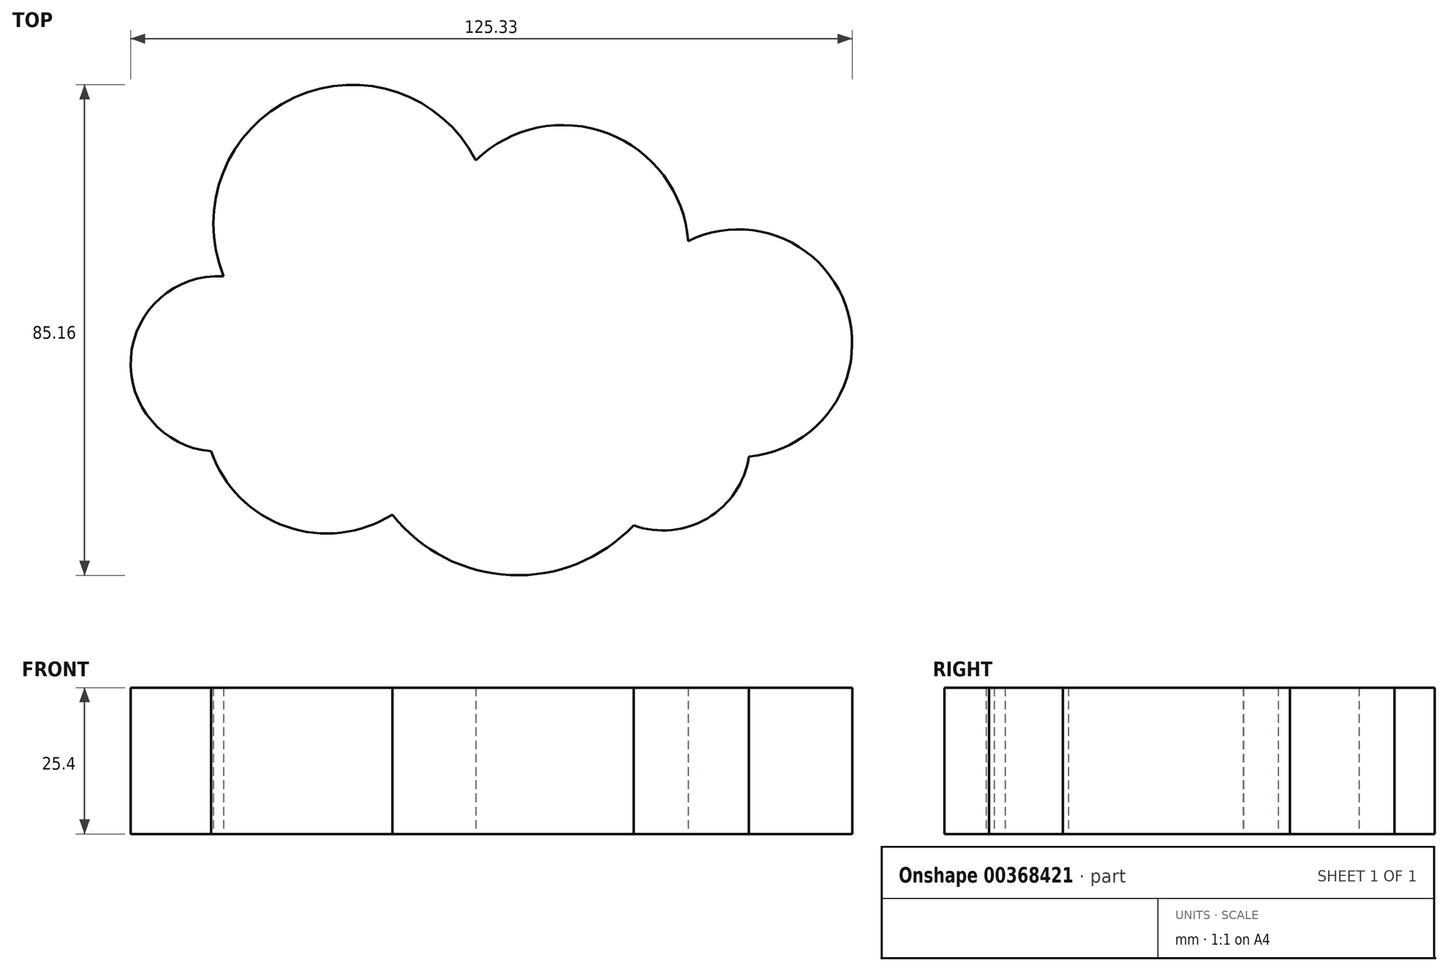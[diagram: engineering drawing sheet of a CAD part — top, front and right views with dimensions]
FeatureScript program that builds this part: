
annotation { "Feature Type Name" : "Feature", "Feature Type Description" : "" }
export const myFeature = defineFeature(function(context is Context, id is Id, definition is map)
    precondition{}
    {
        {
            var Q0;
            Q0=qCreatedBy(makeId("Top.planeOp"),FACE);
            var sketch = newSketch(context, id + "F0", { "sketchPlane" : qUnion([Q0])});
            skArc(sketch, "E0", {"start": v(-17.95, 29.07) * mm, "mid": v(-34.05, 14.96) * mm, "end": v(-20.13, -1.3) * mm});
            skArc(sketch, "E1", {"start": v(25.89, 49.22) * mm, "mid": v(-5.66, 60.1) * mm, "end": v(-17.95, 29.07) * mm});
            skArc(sketch, "E2", {"start": v(-20.13, -1.3) * mm, "mid": v(-7.03, -14.4) * mm, "end": v(11.37, -12.3) * mm});
            skArc(sketch, "E3", {"start": v(11.37, -12.3) * mm, "mid": v(31.9, -22.82) * mm, "end": v(53.27, -14.18) * mm});
            skArc(sketch, "E4", {"start": v(51.92, 14.63) * mm, "mid": v(52, 14.16) * mm, "end": v(52.08, 13.69) * mm});
            skArc(sketch, "E5", {"start": v(53.27, -14.18) * mm, "mid": v(66.12, -12.95) * mm, "end": v(73.3, -2.23) * mm});
            skArc(sketch, "E6.trimOffspring", {"start": v(62.76, 35.17) * mm, "mid": v(48.78, 53.9) * mm, "end": v(25.89, 49.22) * mm});
            skArc(sketch, "E7.trimOffspring", {"start": v(73.3, -2.23) * mm, "mid": v(90.5, 22.8) * mm, "end": v(62.76, 35.17) * mm});
            skSolve(sketch);
        }
        {
            var Q0;
            Q0=makeQuery(id+"F0.imprint","IMPRINT",FACE,{"disambiguationData":[TD([[makeQuery(id+"F0.imprint","IMPRINT",EDGE,{"derivedFrom":sQuery(id+"F0.wireOp",EDGE,"E0")}),1.0]])]});
            extrude(context, id + "F1", {"entities" : qUnion([Q0]), "depth" : 25.4 * mm});
        }
    });
